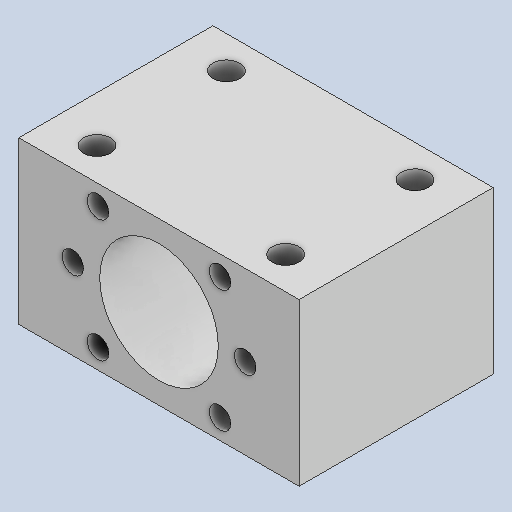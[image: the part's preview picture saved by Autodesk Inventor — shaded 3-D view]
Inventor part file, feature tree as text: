
AUTODESK INVENTOR PART (.ipt)
format: ipt  version: 2023 (Build 270158000, 158)  size: 170,496 bytes
history: native  units: mm
features: extrude x2, sketch x2
ambient origin geometry x8: Origin, YZ Plane, XZ Plane, XY Plane, X Axis, Y Axis, Z Axis, Center Point
bodies: Solid1 (feature_tree)
feature tree (4):
  extrude  "Extrusion1"  Depth=52.0mm
  extrude  "Extrusion3"  Depth=10.0mm
  sketch  "Sketch1"  dims[d0=22.0mm d2=52.0mm]
  sketch  "Sketch3"  dims[d3=32.0mm d4=4.0mm d5=45.0deg d6=15.0mm d9=36.0mm d10=0.0mm d16=30.0mm d17=5.0mm d18=35.0mm d19=24.0mm d20=10.0mm d21=0.0mm]
